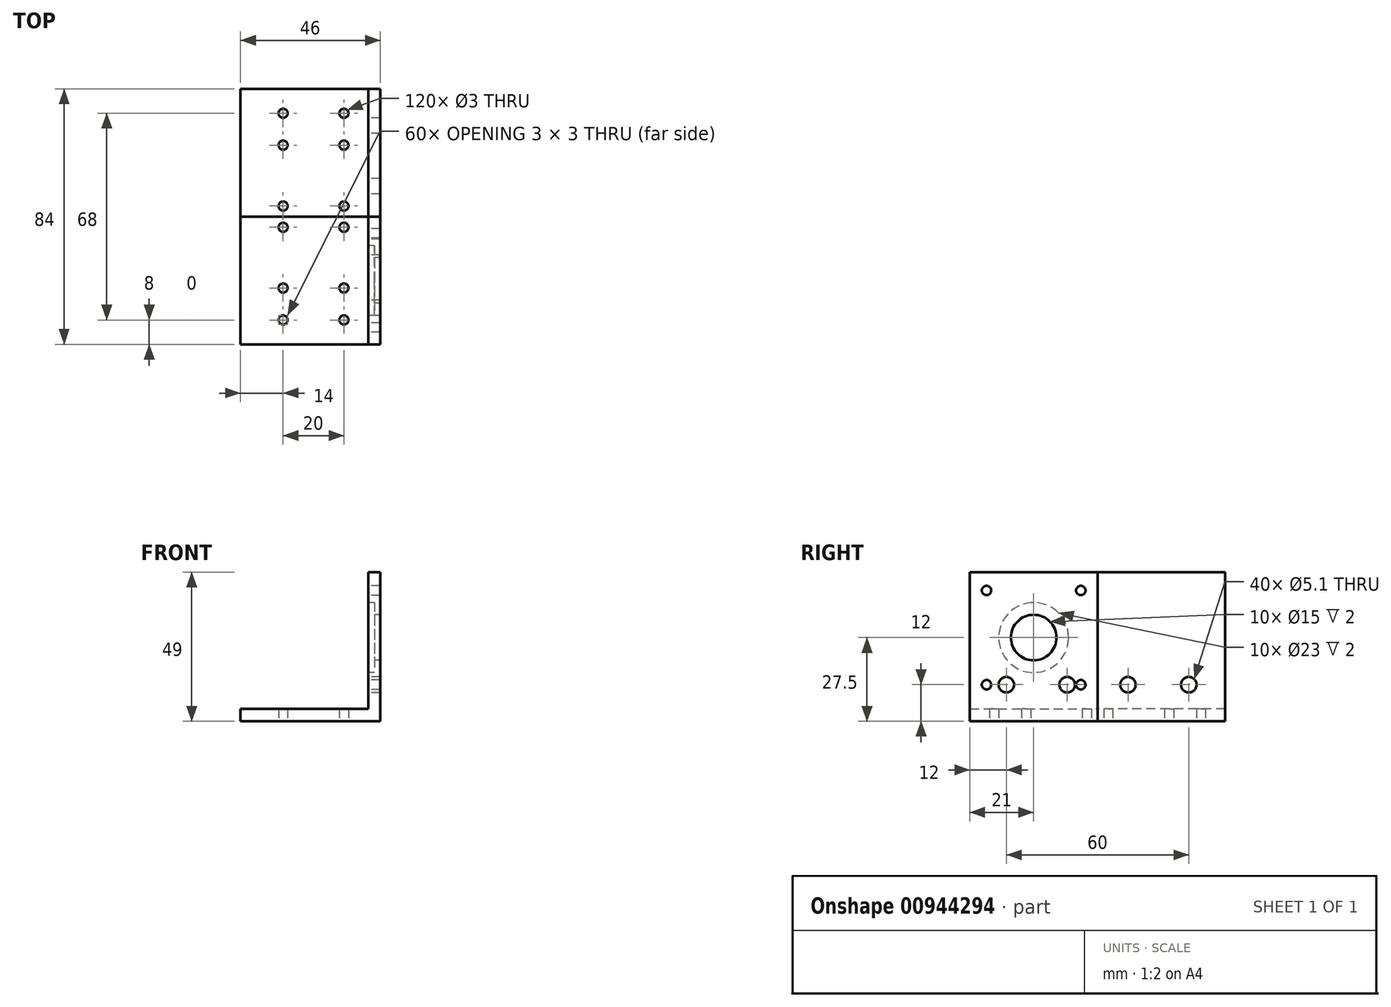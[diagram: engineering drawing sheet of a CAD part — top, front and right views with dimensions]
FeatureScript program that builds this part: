
annotation { "Feature Type Name" : "Feature", "Feature Type Description" : "" }
export const myFeature = defineFeature(function(context is Context, id is Id, definition is map)
    precondition{}
    {
        {
            var Q0;
            Q0=qCreatedBy(makeId("Front.planeOp"),FACE);
            var sketch = newSketch(context, id + "F0", { "sketchPlane" : qUnion([Q0])});
            skLineSegment(sketch, "E0.bottom", {"start": v(0, 0) * mm, "end": v(46, 0) * mm});
            skLineSegment(sketch, "E0.right", {"start": v(46, 0) * mm, "end": v(46, 25) * mm});
            skLineSegment(sketch, "E1.top", {"start": v(0, 4) * mm, "end": v(42, 4) * mm});
            skLineSegment(sketch, "E1.right", {"start": v(42, 23) * mm, "end": v(42, 4) * mm});
            skLineSegment(sketch, "E2", {"start": v(46, 25) * mm, "end": v(46, 49) * mm});
            skLineSegment(sketch, "E3", {"start": v(46, 49) * mm, "end": v(42, 49) * mm});
            skLineSegment(sketch, "E4", {"start": v(42, 49) * mm, "end": v(42, 23) * mm});
            skLineSegment(sketch, "E5", {"start": v(0, 0) * mm, "end": v(0, 4) * mm});
            skSolve(sketch);
        }
        {
            var Q0;
            Q0=makeQuery(id+"F0.imprint","IMPRINT",FACE,{"disambiguationData":[TD([[makeQuery(id+"F0.imprint","IMPRINT",EDGE,{"derivedFrom":sQuery(id+"F0.wireOp",EDGE,"E0.bottom")}),1.0]])]});
            extrude(context, id + "F1", {"entities" : qUnion([Q0]), "depth" : 42 * mm, "offsetDistance" : 25 * mm});
        }
        {
            var Q0;
            Q0=makeQuery(id+"F1.opExtrude","SWEPT_FACE",FACE,{"disambiguationData":[OSD([sQuery(id+"F0.wireOp",EDGE,"E0.bottom")])]});
            var sketch = newSketch(context, id + "F2", { "sketchPlane" : qUnion([Q0])});
            skLineSegment(sketch, "E6", {"start": v(24, 0) * mm, "end": v(24, 42) * mm, "construction": true});
            skLineSegment(sketch, "E7", {"start": v(0, 13.5) * mm, "end": v(46, 13.5) * mm, "construction": true});
            skLineSegment(sketch, "E8", {"start": v(46, 13.5) * mm, "end": v(45.2, 14.22) * mm, "construction": true});
            skCircle(sketch, "E9", {"center": v(14, 3.5) * mm, "radius": 1.5 * mm});
            skCircle(sketch, "E10.MirrorC", {"center": v(34, 3.5) * mm, "radius": 1.5 * mm});
            skCircle(sketch, "E11.MirrorC", {"center": v(14, 23.5) * mm, "radius": 1.5 * mm});
            skCircle(sketch, "E12.MirrorC", {"center": v(34, 23.5) * mm, "radius": 1.5 * mm});
            skLineSegment(sketch, "E13", {"start": v(46, 34) * mm, "end": v(0, 34) * mm, "construction": true});
            skCircle(sketch, "E14", {"center": v(34, 34) * mm, "radius": 1.5 * mm});
            skCircle(sketch, "E15.MirrorC", {"center": v(14, 34) * mm, "radius": 1.5 * mm});
            skSolve(sketch);
        }
        {
            var Q0;
            Q0=qSketchRegion(id+"F2",true);
            extrude(context, id + "F3", {"entities" : qUnion([Q0]), "operationType" : NewBodyOperationType.REMOVE, "oppositeDirection" : true, "depth" : 25 * mm, "offsetDistance" : 25 * mm});
        }
        {
            var Q0;
            Q0=makeQuery(id+"F1.opExtrude","SWEPT_FACE",FACE,{"disambiguationData":[OSD([sQuery(id+"F0.wireOp",EDGE,"E1.right")])]});
            var sketch = newSketch(context, id + "F4", { "sketchPlane" : qUnion([Q0])});
            skLineSegment(sketch, "E16", {"start": v(0, 12) * mm, "end": v(42, 12) * mm, "construction": true});
            skPoint(sketch, "E16.endSnap0", {"position": v(0, 26.5) * mm});
            skCircle(sketch, "E17", {"center": v(10, 12) * mm, "radius": 2.55 * mm});
            skCircle(sketch, "E18", {"center": v(30, 12) * mm, "radius": 2.55 * mm});
            skSolve(sketch);
        }
        {
            var Q0;
            Q0=qSketchRegion(id+"F4",true);
            extrude(context, id + "F5", {"entities" : qUnion([Q0]), "operationType" : NewBodyOperationType.REMOVE, "endBound" : BoundingType.UP_TO_NEXT, "oppositeDirection" : true, "depth" : 25 * mm, "offsetDistance" : 25 * mm});
        }
        {
            var Q0;
            Q0=makeQuery(id+"F1.opExtrude","SWEPT_BODY",BODY,{"disambiguationData":[OSD([sQuery(id+"F0.wireOp",EDGE,"E0.bottom"),sQuery(id+"F0.wireOp",EDGE,"E0.right"),sQuery(id+"F0.wireOp",EDGE,"E1.top"),sQuery(id+"F0.wireOp",EDGE,"E1.right"),sQuery(id+"F0.wireOp",EDGE,"E2"),sQuery(id+"F0.wireOp",EDGE,"E3"),sQuery(id+"F0.wireOp",EDGE,"E4"),sQuery(id+"F0.wireOp",EDGE,"E5")])]});
            var Q1;
            Q1=qCreatedBy(makeId("Front.planeOp"),FACE);
            mirror(context, id + "F6", {"entities" : qUnion([Q0]), "mirrorPlane" : qUnion([Q1])});
        }
        {
            var Q0;
            Q0=makeQuery(id+"F1.opExtrude","SWEPT_FACE",FACE,{"disambiguationData":[OSD([sQuery(id+"F0.wireOp",EDGE,"E1.right"),sQuery(id+"F0.wireOp",EDGE,"E4")])]});
            var sketch = newSketch(context, id + "F7", { "sketchPlane" : qUnion([Q0])});
            skLineSegment(sketch, "E19", {"start": v(21, 49) * mm, "end": v(21, 10) * mm, "construction": true});
            skLineSegment(sketch, "E20", {"start": v(1, 27.5) * mm, "end": v(41, 27.5) * mm, "construction": true});
            skCircle(sketch, "E21", {"center": v(5.5, 43) * mm, "radius": 1.55 * mm});
            skCircle(sketch, "E22.MirrorC", {"center": v(36.5, 43) * mm, "radius": 1.55 * mm});
            skCircle(sketch, "E23.MirrorC", {"center": v(5.5, 12) * mm, "radius": 1.55 * mm});
            skCircle(sketch, "E24.MirrorC", {"center": v(36.5, 12) * mm, "radius": 1.55 * mm});
            skCircle(sketch, "E25", {"center": v(21, 27.5) * mm, "radius": 7.5 * mm});
            skLineSegment(sketch, "E26", {"start": v(10, 12) * mm, "end": v(59.87, 12) * mm, "construction": true});
            skSolve(sketch);
        }
        {
            var Q0;
            Q0=qSketchRegion(id+"F7",true);
            extrude(context, id + "F8", {"entities" : qUnion([Q0]), "operationType" : NewBodyOperationType.REMOVE, "endBound" : BoundingType.THROUGH_ALL, "oppositeDirection" : true, "depth" : 2 * mm, "offsetDistance" : 25 * mm});
        }
        {
            var Q0;
            Q0=makeQuery(id+"F7.imprint","IMPRINT",FACE,{"disambiguationData":[TD([[makeQuery(id+"F7.imprint","IMPRINT",EDGE,{"derivedFrom":sQuery(id+"F7.wireOp",EDGE,"E21")}),-1.0]])]});
            var sketch = newSketch(context, id + "F9", { "sketchPlane" : qUnion([Q0])});
            skLineSegment(sketch, "E27", {"start": v(21, 23.29) * mm, "end": v(21, -26.71) * mm, "construction": true});
            skLineSegment(sketch, "E28", {"start": v(-42.58, 27.5) * mm, "end": v(-2.58, 27.5) * mm, "construction": true});
            skCircle(sketch, "E29", {"center": v(21, 27.5) * mm, "radius": 11.5 * mm});
            skSolve(sketch);
        }
        {
            var Q0;
            Q0=makeQuery(id+"F9.imprint","IMPRINT",FACE,{"disambiguationData":[TD([[makeQuery(id+"F9.imprint","IMPRINT",EDGE,{"derivedFrom":sQuery(id+"F9.wireOp",EDGE,"E29")}),1.0]])]});
            extrude(context, id + "F10", {"entities" : qUnion([Q0]), "operationType" : NewBodyOperationType.REMOVE, "oppositeDirection" : true, "depth" : 2 * mm, "offsetDistance" : 25 * mm});
        }
    });
